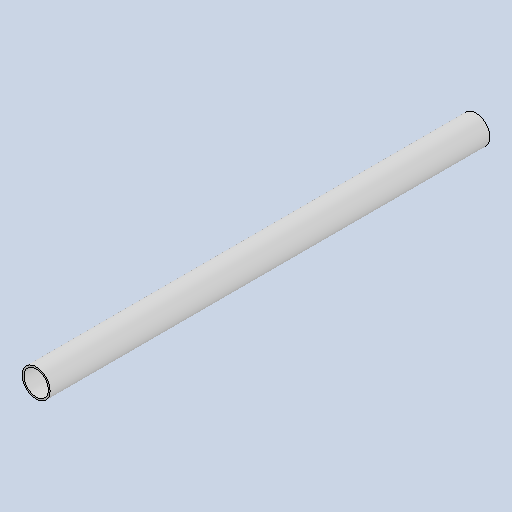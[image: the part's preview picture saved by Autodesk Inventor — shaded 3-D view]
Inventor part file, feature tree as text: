
AUTODESK INVENTOR PART (.ipt)
format: ipt  version: 2025 (Build 290162010, 162A)  size: 90,112 bytes
history: native  units: mm
features: extrude x1
ambient origin geometry x8: Origin, YZ Plane, XZ Plane, XY Plane, X Axis, Y Axis, Z Axis, Center Point
bodies: Solid1 (feature_tree)
feature tree (1):
  extrude  "Extrusion1"  Depth=2.0mm
